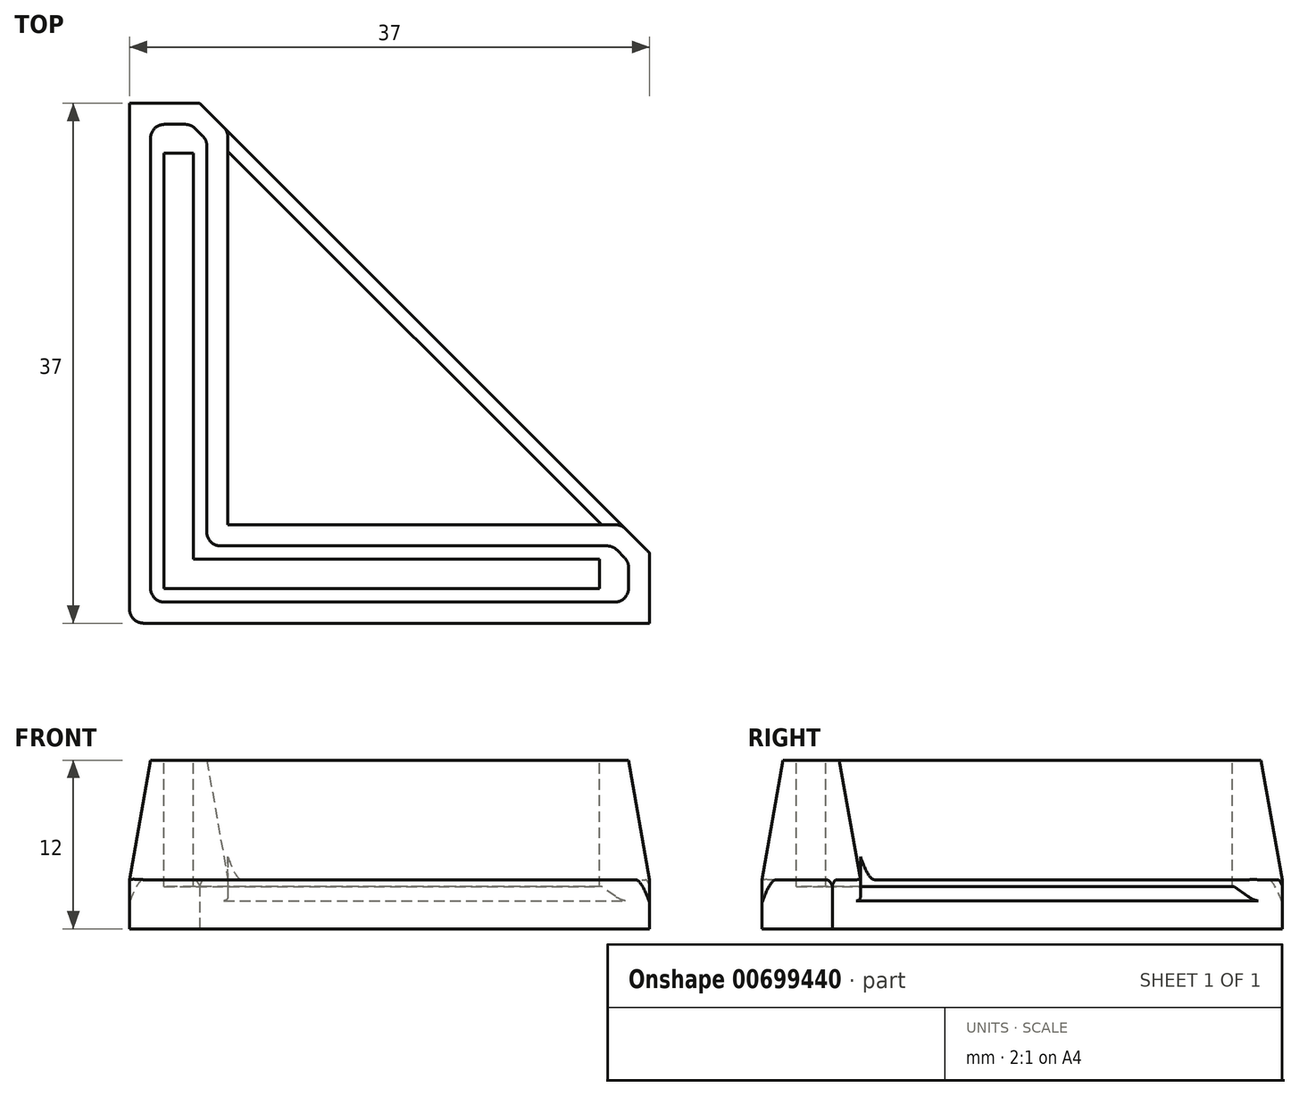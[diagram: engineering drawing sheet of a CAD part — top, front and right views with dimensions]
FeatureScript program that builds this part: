
annotation { "Feature Type Name" : "Feature", "Feature Type Description" : "" }
export const myFeature = defineFeature(function(context is Context, id is Id, definition is map)
    precondition{}
    {
        {
            var Q0;
            Q0=qCreatedBy(makeId("Top.planeOp"),FACE);
            var sketch = newSketch(context, id + "F0", { "sketchPlane" : qUnion([Q0])});
            skLineSegment(sketch, "E0", {"start": v(-42, 42) * mm, "end": v(-42, 0) * mm});
            skLineSegment(sketch, "E1", {"start": v(-42, 0) * mm, "end": v(0, 0) * mm});
            skLineSegment(sketch, "E2", {"start": v(0, 0) * mm, "end": v(-42, 42) * mm});
            skSolve(sketch);
        }
        {
            var Q0;
            Q0=makeQuery(id+"F0.imprint","IMPRINT",FACE,{"disambiguationData":[TD([[makeQuery(id+"F0.imprint","IMPRINT",EDGE,{"derivedFrom":sQuery(id+"F0.wireOp",EDGE,"E0")}),1.0]])]});
            extrude(context, id + "F1", {"entities" : qUnion([Q0]), "depth" : 3 * mm, "offsetDistance" : 25 * mm});
        }
        {
            var Q0;
            Q0=makeQuery(id+"F1.opExtrude","CAP_FACE",FACE,{"disambiguationData":[OSD([sQuery(id+"F0.wireOp",EDGE,"E0"),sQuery(id+"F0.wireOp",EDGE,"E1"),sQuery(id+"F0.wireOp",EDGE,"E2")])],"isStart":false});
            var sketch = newSketch(context, id + "F2", { "sketchPlane" : qUnion([Q0])});
            skLineSegment(sketch, "E3", {"start": v(-42, 0) * mm, "end": v(-5, 0) * mm});
            skLineSegment(sketch, "E4", {"start": v(-5, 0) * mm, "end": v(-5, 5) * mm});
            skLineSegment(sketch, "E5", {"start": v(-7, 7) * mm, "end": v(-35, 7) * mm});
            skLineSegment(sketch, "E6", {"start": v(-35, 7) * mm, "end": v(-35, 35) * mm});
            skLineSegment(sketch, "E7", {"start": v(-37, 37) * mm, "end": v(-42, 37) * mm});
            skLineSegment(sketch, "E8", {"start": v(-42, 37) * mm, "end": v(-42, 0) * mm});
            skLineSegment(sketch, "E9", {"start": v(-5, 5) * mm, "end": v(-7, 7) * mm});
            skLineSegment(sketch, "E10", {"start": v(-35, 35) * mm, "end": v(-37, 37) * mm});
            skSolve(sketch);
        }
        {
            var Q0;
            Q0 = qSketchRegion(id + "F2", true);
            extrude(context, id + "F3", {"entities" : qUnion([Q0]), "operationType" : NewBodyOperationType.ADD, "depth" : 9 * mm, "offsetDistance" : 25 * mm});
        }
        {
            var Q0;
            Q0=makeQuery(id+"F3.opExtrude","CAP_FACE",FACE,{"disambiguationData":[OSD([sQuery(id+"F2.wireOp",EDGE,"E3"),sQuery(id+"F2.wireOp",EDGE,"E4"),sQuery(id+"F2.wireOp",EDGE,"E5"),sQuery(id+"F2.wireOp",EDGE,"E6"),sQuery(id+"F2.wireOp",EDGE,"E7"),sQuery(id+"F2.wireOp",EDGE,"E8")])],"isStart":false});
            var sketch = newSketch(context, id + "F4", { "sketchPlane" : qUnion([Q0])});
            skLineSegment(sketch, "E11", {"start": v(-39.55, 2.45) * mm, "end": v(-8.55, 2.45) * mm});
            skLineSegment(sketch, "E12", {"start": v(-8.55, 2.45) * mm, "end": v(-8.55, 4.55) * mm});
            skLineSegment(sketch, "E13", {"start": v(-8.55, 4.55) * mm, "end": v(-37.45, 4.55) * mm});
            skLineSegment(sketch, "E14", {"start": v(-37.45, 4.55) * mm, "end": v(-37.45, 33.45) * mm});
            skLineSegment(sketch, "E15", {"start": v(-37.45, 33.45) * mm, "end": v(-39.55, 33.45) * mm});
            skLineSegment(sketch, "E16", {"start": v(-39.55, 33.45) * mm, "end": v(-39.55, 2.45) * mm});
            skPoint(sketch, "E17.orphan", {"position": v(-34.73, 2.45) * mm});
            skSolve(sketch);
        }
        {
            var Q0;
            Q0 = qSketchRegion(id + "F4", true);
            extrude(context, id + "F5", {"entities" : qUnion([Q0]), "operationType" : NewBodyOperationType.REMOVE, "oppositeDirection" : true, "depth" : 9 * mm, "offsetDistance" : 25 * mm});
        }
        {
            var Q0;
            {var subQ0=sQuery(id+"F0.wireOp",EDGE,"E2");var subQ1=sQuery(id+"F0.wireOp",EDGE,"E1");Q0=makeQuery(id+"F3.boolean.opBoolean","SPLIT",FACE,{"disambiguationData":[TD([makeQuery(id+"F1.opExtrude","SWEPT_FACE",FACE,{"disambiguationData":[OSD([subQ1])]})])],"derivedFrom":makeQuery(id+"F1.opExtrude","CAP_FACE",FACE,{"disambiguationData":[OSD([sQuery(id+"F0.wireOp",EDGE,"E0"),subQ1,subQ0])],"isStart":false})});}
            var sketch = newSketch(context, id + "F6", { "sketchPlane" : qUnion([Q0])});
            skLineSegment(sketch, "E18", {"start": v(-5, 0) * mm, "end": v(-5, 5) * mm});
            skLineSegment(sketch, "E19", {"start": v(-5, 5) * mm, "end": v(0, 0) * mm});
            skLineSegment(sketch, "E20", {"start": v(0, 0) * mm, "end": v(-5, 0) * mm});
            skSolve(sketch);
        }
        {
            var Q0;
            Q0 = qSketchRegion(id + "F6", true);
            extrude(context, id + "F7", {"entities" : qUnion([Q0]), "operationType" : NewBodyOperationType.REMOVE, "oppositeDirection" : true, "depth" : 25 * mm, "offsetDistance" : 25 * mm});
        }
        {
            var Q0;
            {var subQ0=sQuery(id+"F0.wireOp",EDGE,"E2");var subQ1=sQuery(id+"F0.wireOp",EDGE,"E0");Q0=makeQuery(id+"F3.boolean.opBoolean","SPLIT",FACE,{"disambiguationData":[TD([makeQuery(id+"F1.opExtrude","SWEPT_FACE",FACE,{"disambiguationData":[OSD([subQ1])]})])],"derivedFrom":makeQuery(id+"F1.opExtrude","CAP_FACE",FACE,{"disambiguationData":[OSD([subQ1,sQuery(id+"F0.wireOp",EDGE,"E1"),subQ0])],"isStart":false})});}
            var sketch = newSketch(context, id + "F8", { "sketchPlane" : qUnion([Q0])});
            skLineSegment(sketch, "E21", {"start": v(-42, 37) * mm, "end": v(-37, 37) * mm});
            skLineSegment(sketch, "E22", {"start": v(-37, 37) * mm, "end": v(-42, 42) * mm});
            skLineSegment(sketch, "E23", {"start": v(-42, 42) * mm, "end": v(-42, 37) * mm});
            skSolve(sketch);
        }
        {
            var Q0;
            Q0 = qSketchRegion(id + "F8", true);
            extrude(context, id + "F9", {"entities" : qUnion([Q0]), "operationType" : NewBodyOperationType.REMOVE, "oppositeDirection" : true, "depth" : 25 * mm, "offsetDistance" : 25 * mm});
        }
        {
            var Q0;
            Q0=makeQuery(id+"F3.opExtrude","CAP_EDGE",EDGE,{"disambiguationData":[OSD([sQuery(id+"F2.wireOp",EDGE,"E3")])],"isStart":false});
            var Q1;
            Q1=makeQuery(id+"F3.opExtrude","CAP_EDGE",EDGE,{"disambiguationData":[OSD([sQuery(id+"F2.wireOp",EDGE,"E4")])],"isStart":false});
            var Q2;
            Q2=makeQuery(id+"F3.opExtrude","CAP_EDGE",EDGE,{"disambiguationData":[OSD([sQuery(id+"F2.wireOp",EDGE,"E9")])],"isStart":false});
            var Q3;
            Q3=makeQuery(id+"F3.opExtrude","CAP_EDGE",EDGE,{"disambiguationData":[OSD([sQuery(id+"F2.wireOp",EDGE,"E5")])],"isStart":false});
            var Q4;
            Q4=makeQuery(id+"F3.opExtrude","CAP_EDGE",EDGE,{"disambiguationData":[OSD([sQuery(id+"F2.wireOp",EDGE,"E6")])],"isStart":false});
            var Q5;
            Q5=makeQuery(id+"F3.opExtrude","CAP_EDGE",EDGE,{"disambiguationData":[OSD([sQuery(id+"F2.wireOp",EDGE,"E10")])],"isStart":false});
            var Q6;
            Q6=makeQuery(id+"F3.opExtrude","CAP_EDGE",EDGE,{"disambiguationData":[OSD([sQuery(id+"F2.wireOp",EDGE,"E7")])],"isStart":false});
            var Q7;
            Q7=makeQuery(id+"F3.opExtrude","CAP_EDGE",EDGE,{"disambiguationData":[OSD([sQuery(id+"F2.wireOp",EDGE,"E8")])],"isStart":false});
            chamfer(context, id + "F10", {"entities" : qUnion([Q0, Q1, Q2, Q3, Q4, Q5, Q6, Q7]), "chamferType" : ChamferType.OFFSET_ANGLE, "width" : 1.5 * mm, "oppositeDirection" : false, "angle" : 80 * degree, "tangentPropagation" : true});
        }
        {
            var Q0;
            {var subQ0=sQuery(id+"F0.wireOp",EDGE,"E2");Q0=makeQuery(id+"F3.boolean.opBoolean","SPLIT",EDGE,{"disambiguationData":[TD([makeQuery(id+"F3.opExtrude","SWEPT_FACE",FACE,{"disambiguationData":[OSD([sQuery(id+"F2.wireOp",EDGE,"E5")])]})])],"derivedFrom":makeQuery(id+"F1.opExtrude","CAP_EDGE",EDGE,{"disambiguationData":[OSD([subQ0])],"isStart":false})});}
            chamfer(context, id + "F11", {"entities" : qUnion([Q0]), "width" : 1 * mm, "tangentPropagation" : true});
        }
        {
            var Q0;
            Q0=makeQuery(id+"F7.boolean.opBoolean","MERGE",EDGE,{"derivedFrom":[makeQuery(id+"F3.opExtrude","SWEPT_EDGE",EDGE,{"disambiguationData":[OSD([sQuery(id+"F0.wireOp",EDGE,"E1"),sQuery(id+"F2.wireOp",EDGE,"E3"),sQuery(id+"F2.wireOp",EDGE,"E4")])]}),makeQuery(id+"F7.opExtrude","SWEPT_EDGE",EDGE,{"disambiguationData":[OSD([sQuery(id+"F6.wireOp",EDGE,"E18"),sQuery(id+"F6.wireOp",EDGE,"E20")])]})]});
            var Q1;
            Q1=makeQuery(id+"F7.boolean.opBoolean","MERGE",EDGE,{"derivedFrom":[makeQuery(id+"F3.opExtrude","SWEPT_EDGE",EDGE,{"disambiguationData":[OSD([sQuery(id+"F0.wireOp",EDGE,"E2"),sQuery(id+"F2.wireOp",EDGE,"E4"),sQuery(id+"F2.wireOp",EDGE,"E9")])]}),makeQuery(id+"F7.opExtrude","SWEPT_EDGE",EDGE,{"disambiguationData":[OSD([sQuery(id+"F6.wireOp",EDGE,"E18"),sQuery(id+"F6.wireOp",EDGE,"E19")])]})]});
            var Q2;
            Q2=makeQuery(id+"F9.boolean.opBoolean","MERGE",EDGE,{"derivedFrom":[makeQuery(id+"F3.opExtrude","SWEPT_EDGE",EDGE,{"disambiguationData":[OSD([sQuery(id+"F0.wireOp",EDGE,"E2"),sQuery(id+"F2.wireOp",EDGE,"E7"),sQuery(id+"F2.wireOp",EDGE,"E10")])]}),makeQuery(id+"F9.opExtrude","SWEPT_EDGE",EDGE,{"disambiguationData":[OSD([sQuery(id+"F8.wireOp",EDGE,"E21"),sQuery(id+"F8.wireOp",EDGE,"E22")])]})]});
            var Q3;
            Q3=makeQuery(id+"F9.boolean.opBoolean","MERGE",EDGE,{"derivedFrom":[makeQuery(id+"F3.opExtrude","SWEPT_EDGE",EDGE,{"disambiguationData":[OSD([sQuery(id+"F0.wireOp",EDGE,"E0"),sQuery(id+"F2.wireOp",EDGE,"E7"),sQuery(id+"F2.wireOp",EDGE,"E8")])]}),makeQuery(id+"F9.opExtrude","SWEPT_EDGE",EDGE,{"disambiguationData":[OSD([sQuery(id+"F8.wireOp",EDGE,"E21"),sQuery(id+"F8.wireOp",EDGE,"E23")])]})]});
            var Q4;
            Q4=makeQuery(id+"F3.boolean.opBoolean","MERGE",EDGE,{"derivedFrom":[makeQuery(id+"F1.opExtrude","SWEPT_EDGE",EDGE,{"disambiguationData":[OSD([sQuery(id+"F0.wireOp",EDGE,"E0"),sQuery(id+"F0.wireOp",EDGE,"E1")])]}),makeQuery(id+"F3.opExtrude","SWEPT_EDGE",EDGE,{"disambiguationData":[OSD([sQuery(id+"F2.wireOp",EDGE,"E3"),sQuery(id+"F2.wireOp",EDGE,"E8")])]})]});
            var Q5;
            Q5=makeQuery(id+"F10.opChamfer","BLEND_EDGE",EDGE,{"blendedFrom":[makeQuery(id+"F3.opExtrude","CAP_EDGE",EDGE,{"disambiguationData":[OSD([sQuery(id+"F2.wireOp",EDGE,"E3")])],"isStart":false}),makeQuery(id+"F3.opExtrude","CAP_EDGE",EDGE,{"disambiguationData":[OSD([sQuery(id+"F2.wireOp",EDGE,"E4")])],"isStart":false})],"blendedInto":[]});
            var Q6;
            Q6=makeQuery(id+"F10.opChamfer","BLEND_EDGE",EDGE,{"blendedFrom":[makeQuery(id+"F3.opExtrude","CAP_EDGE",EDGE,{"disambiguationData":[OSD([sQuery(id+"F2.wireOp",EDGE,"E4")])],"isStart":false}),makeQuery(id+"F3.opExtrude","CAP_EDGE",EDGE,{"disambiguationData":[OSD([sQuery(id+"F2.wireOp",EDGE,"E9")])],"isStart":false})],"blendedInto":[]});
            var Q7;
            Q7=makeQuery(id+"F10.opChamfer","BLEND_EDGE",EDGE,{"blendedFrom":[makeQuery(id+"F3.opExtrude","CAP_EDGE",EDGE,{"disambiguationData":[OSD([sQuery(id+"F2.wireOp",EDGE,"E5")])],"isStart":false}),makeQuery(id+"F3.opExtrude","CAP_EDGE",EDGE,{"disambiguationData":[OSD([sQuery(id+"F2.wireOp",EDGE,"E9")])],"isStart":false})],"blendedInto":[]});
            var Q8;
            Q8=makeQuery(id+"F10.opChamfer","BLEND_EDGE",EDGE,{"blendedFrom":[makeQuery(id+"F3.opExtrude","CAP_EDGE",EDGE,{"disambiguationData":[OSD([sQuery(id+"F2.wireOp",EDGE,"E6")])],"isStart":false}),makeQuery(id+"F3.opExtrude","CAP_EDGE",EDGE,{"disambiguationData":[OSD([sQuery(id+"F2.wireOp",EDGE,"E10")])],"isStart":false})],"blendedInto":[]});
            var Q9;
            Q9=makeQuery(id+"F10.opChamfer","BLEND_EDGE",EDGE,{"blendedFrom":[makeQuery(id+"F3.opExtrude","CAP_EDGE",EDGE,{"disambiguationData":[OSD([sQuery(id+"F2.wireOp",EDGE,"E7")])],"isStart":false}),makeQuery(id+"F3.opExtrude","CAP_EDGE",EDGE,{"disambiguationData":[OSD([sQuery(id+"F2.wireOp",EDGE,"E10")])],"isStart":false})],"blendedInto":[]});
            var Q10;
            Q10=makeQuery(id+"F10.opChamfer","BLEND_EDGE",EDGE,{"blendedFrom":[makeQuery(id+"F3.opExtrude","CAP_EDGE",EDGE,{"disambiguationData":[OSD([sQuery(id+"F2.wireOp",EDGE,"E7")])],"isStart":false}),makeQuery(id+"F3.opExtrude","CAP_EDGE",EDGE,{"disambiguationData":[OSD([sQuery(id+"F2.wireOp",EDGE,"E8")])],"isStart":false})],"blendedInto":[]});
            var Q11;
            Q11=makeQuery(id+"F10.opChamfer","BLEND_EDGE",EDGE,{"blendedFrom":[makeQuery(id+"F3.opExtrude","CAP_EDGE",EDGE,{"disambiguationData":[OSD([sQuery(id+"F2.wireOp",EDGE,"E3")])],"isStart":false}),makeQuery(id+"F3.opExtrude","CAP_EDGE",EDGE,{"disambiguationData":[OSD([sQuery(id+"F2.wireOp",EDGE,"E8")])],"isStart":false})],"blendedInto":[]});
            var Q12;
            Q12=makeQuery(id+"F10.opChamfer","BLEND_EDGE",EDGE,{"blendedFrom":[makeQuery(id+"F3.opExtrude","CAP_EDGE",EDGE,{"disambiguationData":[OSD([sQuery(id+"F2.wireOp",EDGE,"E5")])],"isStart":false}),makeQuery(id+"F3.opExtrude","CAP_EDGE",EDGE,{"disambiguationData":[OSD([sQuery(id+"F2.wireOp",EDGE,"E6")])],"isStart":false})],"blendedInto":[]});
            var Q13;
            Q13=makeQuery(id+"F3.opExtrude","SWEPT_EDGE",EDGE,{"disambiguationData":[OSD([sQuery(id+"F0.wireOp",EDGE,"E2"),sQuery(id+"F2.wireOp",EDGE,"E5"),sQuery(id+"F2.wireOp",EDGE,"E9")])]});
            var Q14;
            Q14=makeQuery(id+"F3.opExtrude","SWEPT_EDGE",EDGE,{"disambiguationData":[OSD([sQuery(id+"F0.wireOp",EDGE,"E2"),sQuery(id+"F2.wireOp",EDGE,"E6"),sQuery(id+"F2.wireOp",EDGE,"E10")])]});
            fillet(context, id + "F12", {"entities" : qUnion([Q0, Q1, Q2, Q3, Q4, Q5, Q6, Q7, Q8, Q9, Q10, Q11, Q12, Q13, Q14]), "radius" : 1 * mm, "tangentPropagation" : true, "allowEdgeOverflow" : false});
        }
    });
